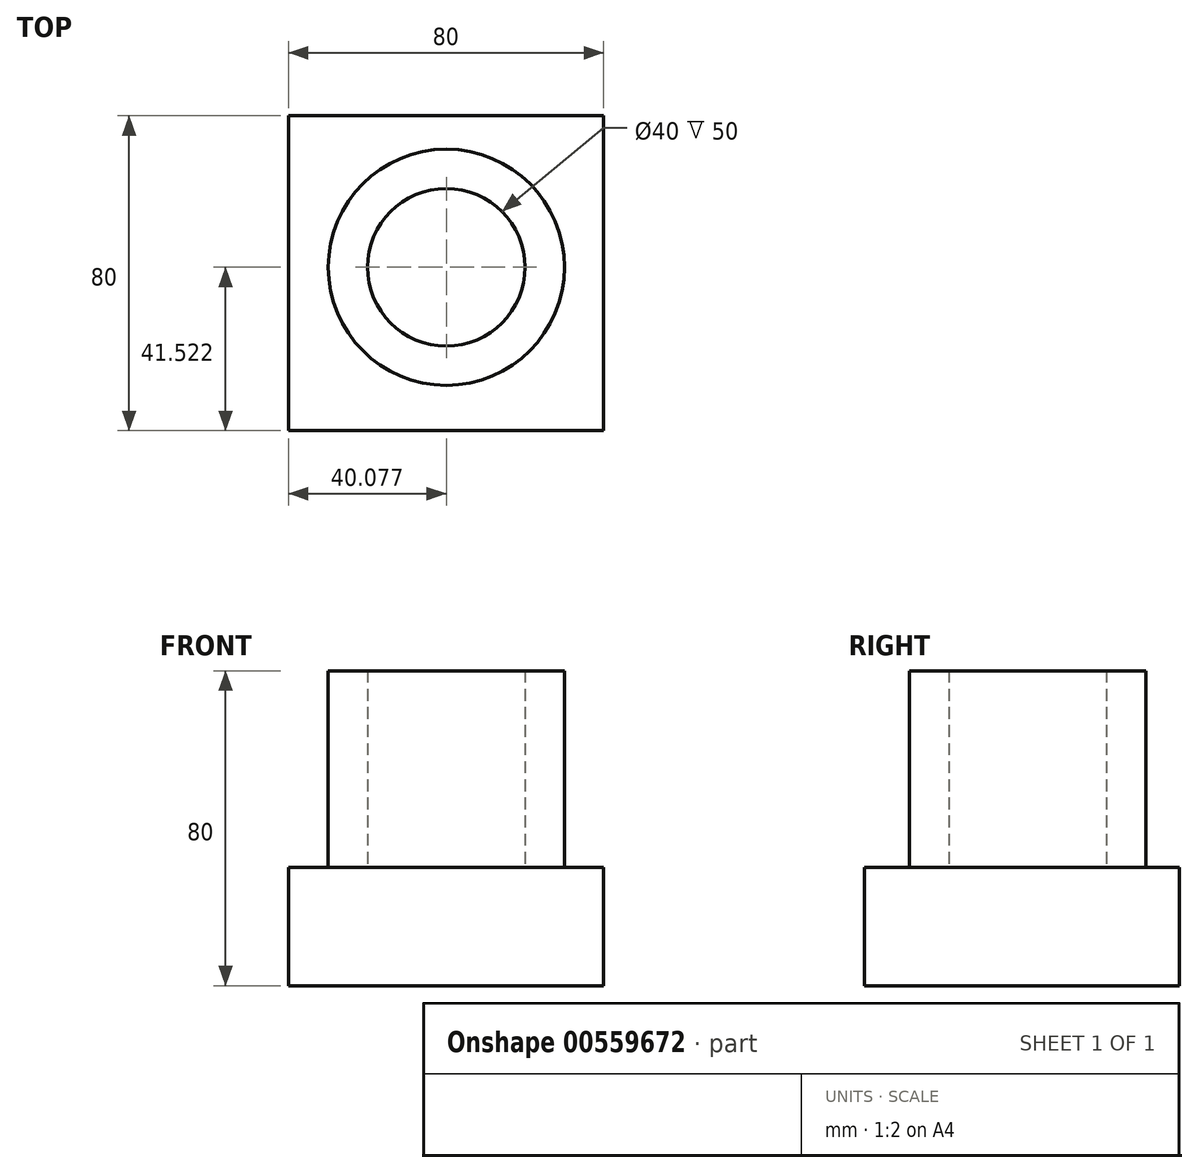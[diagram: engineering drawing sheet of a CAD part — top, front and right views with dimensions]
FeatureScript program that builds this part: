
annotation { "Feature Type Name" : "Feature", "Feature Type Description" : "" }
export const myFeature = defineFeature(function(context is Context, id is Id, definition is map)
    precondition{}
    {
        {
            var Q0;
            Q0=qCreatedBy(makeId("Front.planeOp"),FACE);
            var sketch = newSketch(context, id + "F0", { "sketchPlane" : qUnion([Q0])});
            skLineSegment(sketch, "E0.bottom", {"start": v(-40, 15) * mm, "end": v(40, 15) * mm});
            skLineSegment(sketch, "E0.top", {"start": v(-40, -15) * mm, "end": v(40, -15) * mm});
            skLineSegment(sketch, "E0.left", {"start": v(-40, 15) * mm, "end": v(-40, -15) * mm});
            skLineSegment(sketch, "E0.right", {"start": v(40, 15) * mm, "end": v(40, -15) * mm});
            skPoint(sketch, "E0.middle", {"position": v(0, 0) * mm});
            skSolve(sketch);
        }
        {
            var Q0;
            Q0=makeQuery(id+"F0.imprint","IMPRINT",FACE,{"disambiguationData":[TD([[makeQuery(id+"F0.imprint","IMPRINT",EDGE,{"derivedFrom":sQuery(id+"F0.wireOp",EDGE,"E0.bottom")}),-1.0]])]});
            var Q1;
            Q1=makeQuery(id+"F0.imprint","IMPRINT",FACE,{"disambiguationData":[TD([[makeQuery(id+"F0.imprint","IMPRINT",EDGE,{"derivedFrom":sQuery(id+"F0.wireOp",EDGE,"E0.bottom")}),-1.0]])]});
            extrude(context, id + "F1", {"entities" : qUnion([Q0, Q1]), "depth" : 80 * mm, "offsetDistance" : 25.4 * mm});
        }
        {
            var Q0;
            Q0=makeQuery(id+"F1.opExtrude","SWEPT_FACE",FACE,{"disambiguationData":[OSD([sQuery(id+"F0.wireOp",EDGE,"E0.bottom")])]});
            var sketch = newSketch(context, id + "F2", { "sketchPlane" : qUnion([Q0])});
            skCircle(sketch, "E1", {"center": v(0.08, -38.48) * mm, "radius": 30 * mm});
            skCircle(sketch, "E2", {"center": v(0.08, -38.48) * mm, "radius": 20 * mm});
            skSolve(sketch);
        }
        {
            var Q0;
            Q0 = qSketchRegion(id + "F2", true);
            extrude(context, id + "F3", {"entities" : qUnion([Q0]), "operationType" : NewBodyOperationType.ADD, "depth" : 50 * mm, "offsetDistance" : 25.4 * mm});
        }
    });
